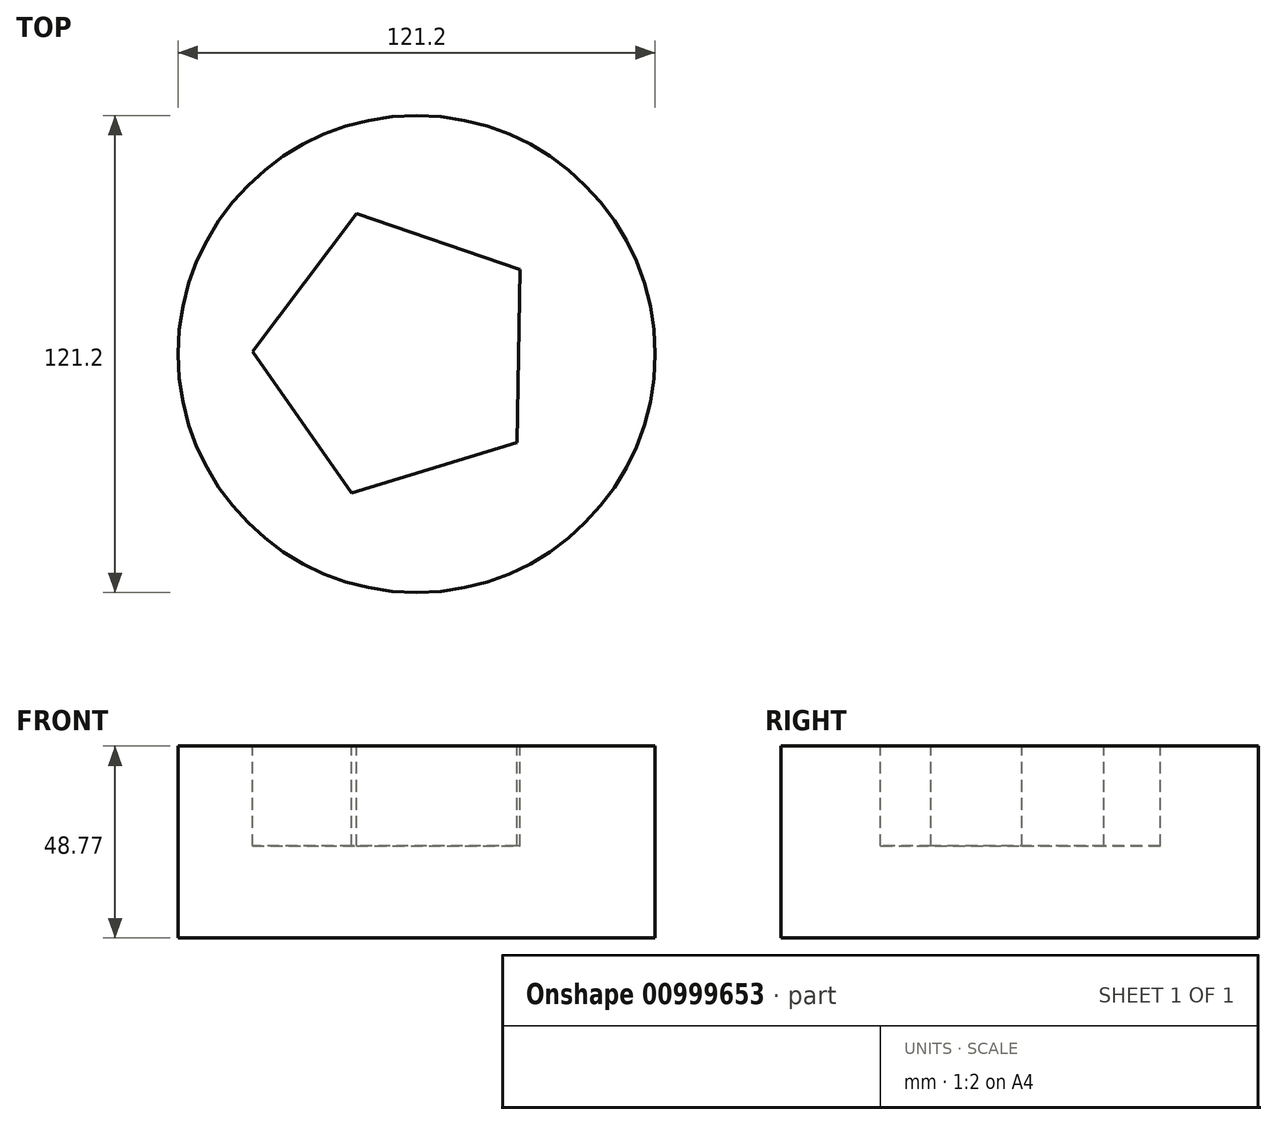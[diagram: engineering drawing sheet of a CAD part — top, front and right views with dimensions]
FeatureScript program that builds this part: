
annotation { "Feature Type Name" : "Feature", "Feature Type Description" : "" }
export const myFeature = defineFeature(function(context is Context, id is Id, definition is map)
    precondition{}
    {
        {
            var Q0;
            Q0=qCreatedBy(makeId("Top.planeOp"),FACE);
            var sketch = newSketch(context, id + "F0", { "sketchPlane" : qUnion([Q0])});
            skCircle(sketch, "E0", {"center": v(0, 0) * mm, "radius": 60.6 * mm});
            skSolve(sketch);
        }
        {
            var Q0;
            Q0=makeQuery(id+"F0.imprint","IMPRINT",FACE,{"disambiguationData":[TD([[makeQuery(id+"F0.imprint","IMPRINT",EDGE,{"derivedFrom":sQuery(id+"F0.wireOp",EDGE,"E0")}),1.0]])]});
            extrude(context, id + "F1", {"entities" : qUnion([Q0]), "depth" : 48.77 * mm, "offsetDistance" : 25.4 * mm});
        }
        {
            var Q0;
            Q0=makeQuery(id+"F1.opExtrude","CAP_FACE",FACE,{"disambiguationData":[OSD([sQuery(id+"F0.wireOp",EDGE,"E0")])],"isStart":false});
            var sketch = newSketch(context, id + "F2", { "sketchPlane" : qUnion([Q0])});
            skCircle(sketch, "E1.cCircle", {"center": v(-4.34, 0) * mm, "radius": 30.22 * mm, "construction": true});
            skLineSegment(sketch, "E1.0", {"start": v(-41.7, 0.65) * mm, "end": v(-15.27, 35.72) * mm});
            skLineSegment(sketch, "E1.1", {"start": v(-15.27, 35.72) * mm, "end": v(26.25, 21.43) * mm});
            skLineSegment(sketch, "E1.2", {"start": v(26.25, 21.43) * mm, "end": v(25.49, -22.47) * mm});
            skLineSegment(sketch, "E1.3", {"start": v(25.49, -22.47) * mm, "end": v(-16.5, -35.32) * mm});
            skLineSegment(sketch, "E1.4", {"start": v(-16.5, -35.32) * mm, "end": v(-41.7, 0.65) * mm});
            skPoint(sketch, "E1.0.midPoint", {"position": v(-28.48, 18.18) * mm});
            skSolve(sketch);
        }
        {
            var Q0;
            Q0=makeQuery(id+"F2.imprint","IMPRINT",FACE,{"disambiguationData":[TD([[makeQuery(id+"F2.imprint","IMPRINT",EDGE,{"derivedFrom":sQuery(id+"F2.wireOp",EDGE,"E1.0")}),-1.0]])]});
            extrude(context, id + "F3", {"entities" : qUnion([Q0]), "operationType" : NewBodyOperationType.REMOVE, "oppositeDirection" : true, "depth" : 25.4 * mm, "offsetDistance" : 25.4 * mm});
        }
    });
